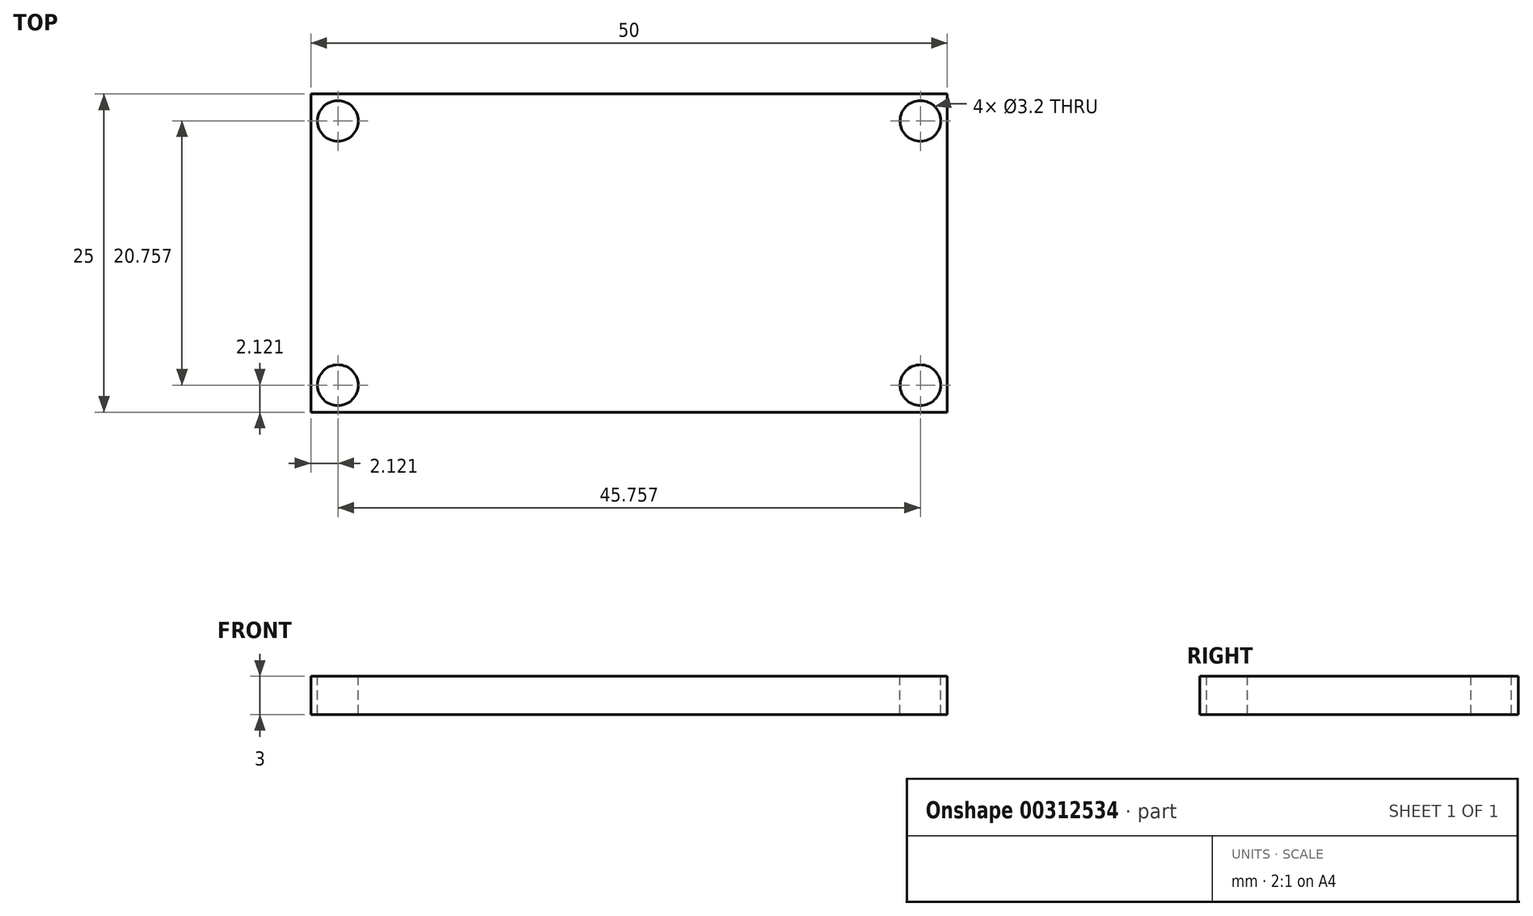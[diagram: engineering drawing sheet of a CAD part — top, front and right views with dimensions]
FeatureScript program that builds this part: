
annotation { "Feature Type Name" : "Feature", "Feature Type Description" : "" }
export const myFeature = defineFeature(function(context is Context, id is Id, definition is map)
    precondition{}
    {
        {
            var Q0;
            Q0=qCreatedBy(makeId("Top.planeOp"),FACE);
            var sketch = newSketch(context, id + "F0", { "sketchPlane" : qUnion([Q0])});
            skLineSegment(sketch, "E0.bottom", {"start": v(0, 0) * mm, "end": v(50, 0) * mm});
            skLineSegment(sketch, "E0.top", {"start": v(0, 25) * mm, "end": v(50, 25) * mm});
            skLineSegment(sketch, "E0.left", {"start": v(0, 0) * mm, "end": v(0, 25) * mm});
            skLineSegment(sketch, "E0.right", {"start": v(50, 0) * mm, "end": v(50, 25) * mm});
            skSolve(sketch);
        }
        {
            var Q0;
            Q0=makeQuery(id+"F0.imprint","IMPRINT",FACE,{"disambiguationData":[TD([[makeQuery(id+"F0.imprint","IMPRINT",EDGE,{"derivedFrom":sQuery(id+"F0.wireOp",EDGE,"E0.bottom")}),1.0]])]});
            extrude(context, id + "F1", {"entities" : qUnion([Q0]), "depth" : 3 * mm});
        }
        {
            var Q0;
            Q0=makeQuery(id+"F1.opExtrude","CAP_FACE",FACE,{"disambiguationData":[OSD([sQuery(id+"F0.wireOp",EDGE,"E0.bottom"),sQuery(id+"F0.wireOp",EDGE,"E0.top"),sQuery(id+"F0.wireOp",EDGE,"E0.left"),sQuery(id+"F0.wireOp",EDGE,"E0.right")])],"isStart":false});
            var sketch = newSketch(context, id + "F2", { "sketchPlane" : qUnion([Q0])});
            skLineSegment(sketch, "E1", {"start": v(0, 25) * mm, "end": v(2.12, 22.88) * mm});
            skLineSegment(sketch, "E2", {"start": v(0, 25) * mm, "end": v(18.13, 25) * mm});
            skLineSegment(sketch, "E3", {"start": v(0, 0) * mm, "end": v(0, 6.4) * mm});
            skLineSegment(sketch, "E4", {"start": v(0, 0) * mm, "end": v(2.12, 2.12) * mm});
            skLineSegment(sketch, "E5", {"start": v(50, 25) * mm, "end": v(50, 19.22) * mm});
            skLineSegment(sketch, "E6", {"start": v(50, 25) * mm, "end": v(47.88, 22.88) * mm});
            skLineSegment(sketch, "E7", {"start": v(50, 0) * mm, "end": v(50, 4.41) * mm});
            skLineSegment(sketch, "E8", {"start": v(50, 0) * mm, "end": v(47.88, 2.12) * mm});
            skSolve(sketch);
        }
        {
            var Q0;
            Q0=sQuery(id+"F2.wireOp",VERTEX,"E1.end");
            var Q1;
            Q1=makeQuery(id+"F1.opExtrude","SWEPT_BODY",BODY,{"disambiguationData":[OSD([sQuery(id+"F0.wireOp",EDGE,"E0.bottom"),sQuery(id+"F0.wireOp",EDGE,"E0.top"),sQuery(id+"F0.wireOp",EDGE,"E0.left"),sQuery(id+"F0.wireOp",EDGE,"E0.right")])]});
            hole(context, id + "F3", {"style" : HoleStyle.SIMPLE, "endStyle" : HoleEndStyle.THROUGH, "holeDiameter" : 3.2 * mm, "tappedDepth" : 12 * mm, "tapClearance" : 3, "locations" : qUnion([Q0]), "scope" : qUnion([Q1])});
        }
        {
            var Q0;
            Q0=sQuery(id+"F2.wireOp",VERTEX,"E4.end");
            var Q1;
            Q1=makeQuery(id+"F1.opExtrude","SWEPT_BODY",BODY,{"disambiguationData":[OSD([sQuery(id+"F0.wireOp",EDGE,"E0.bottom"),sQuery(id+"F0.wireOp",EDGE,"E0.top"),sQuery(id+"F0.wireOp",EDGE,"E0.left"),sQuery(id+"F0.wireOp",EDGE,"E0.right")])]});
            hole(context, id + "F4", {"style" : HoleStyle.SIMPLE, "endStyle" : HoleEndStyle.THROUGH, "holeDiameter" : 3.2 * mm, "tappedDepth" : 12 * mm, "tapClearance" : 3, "locations" : qUnion([Q0]), "scope" : qUnion([Q1])});
        }
        {
            var Q0;
            Q0=sQuery(id+"F2.wireOp",VERTEX,"E8.end");
            var Q1;
            Q1=makeQuery(id+"F1.opExtrude","SWEPT_BODY",BODY,{"disambiguationData":[OSD([sQuery(id+"F0.wireOp",EDGE,"E0.bottom"),sQuery(id+"F0.wireOp",EDGE,"E0.top"),sQuery(id+"F0.wireOp",EDGE,"E0.left"),sQuery(id+"F0.wireOp",EDGE,"E0.right")])]});
            hole(context, id + "F5", {"style" : HoleStyle.SIMPLE, "endStyle" : HoleEndStyle.THROUGH, "holeDiameter" : 3.2 * mm, "tappedDepth" : 12 * mm, "tapClearance" : 3, "locations" : qUnion([Q0]), "scope" : qUnion([Q1])});
        }
        {
            var Q0;
            Q0=sQuery(id+"F2.wireOp",VERTEX,"E6.end");
            var Q1;
            Q1=makeQuery(id+"F1.opExtrude","SWEPT_BODY",BODY,{"disambiguationData":[OSD([sQuery(id+"F0.wireOp",EDGE,"E0.bottom"),sQuery(id+"F0.wireOp",EDGE,"E0.top"),sQuery(id+"F0.wireOp",EDGE,"E0.left"),sQuery(id+"F0.wireOp",EDGE,"E0.right")])]});
            hole(context, id + "F6", {"style" : HoleStyle.SIMPLE, "endStyle" : HoleEndStyle.THROUGH, "holeDiameter" : 3.2 * mm, "tappedDepth" : 12 * mm, "tapClearance" : 3, "locations" : qUnion([Q0]), "scope" : qUnion([Q1])});
        }
    });
